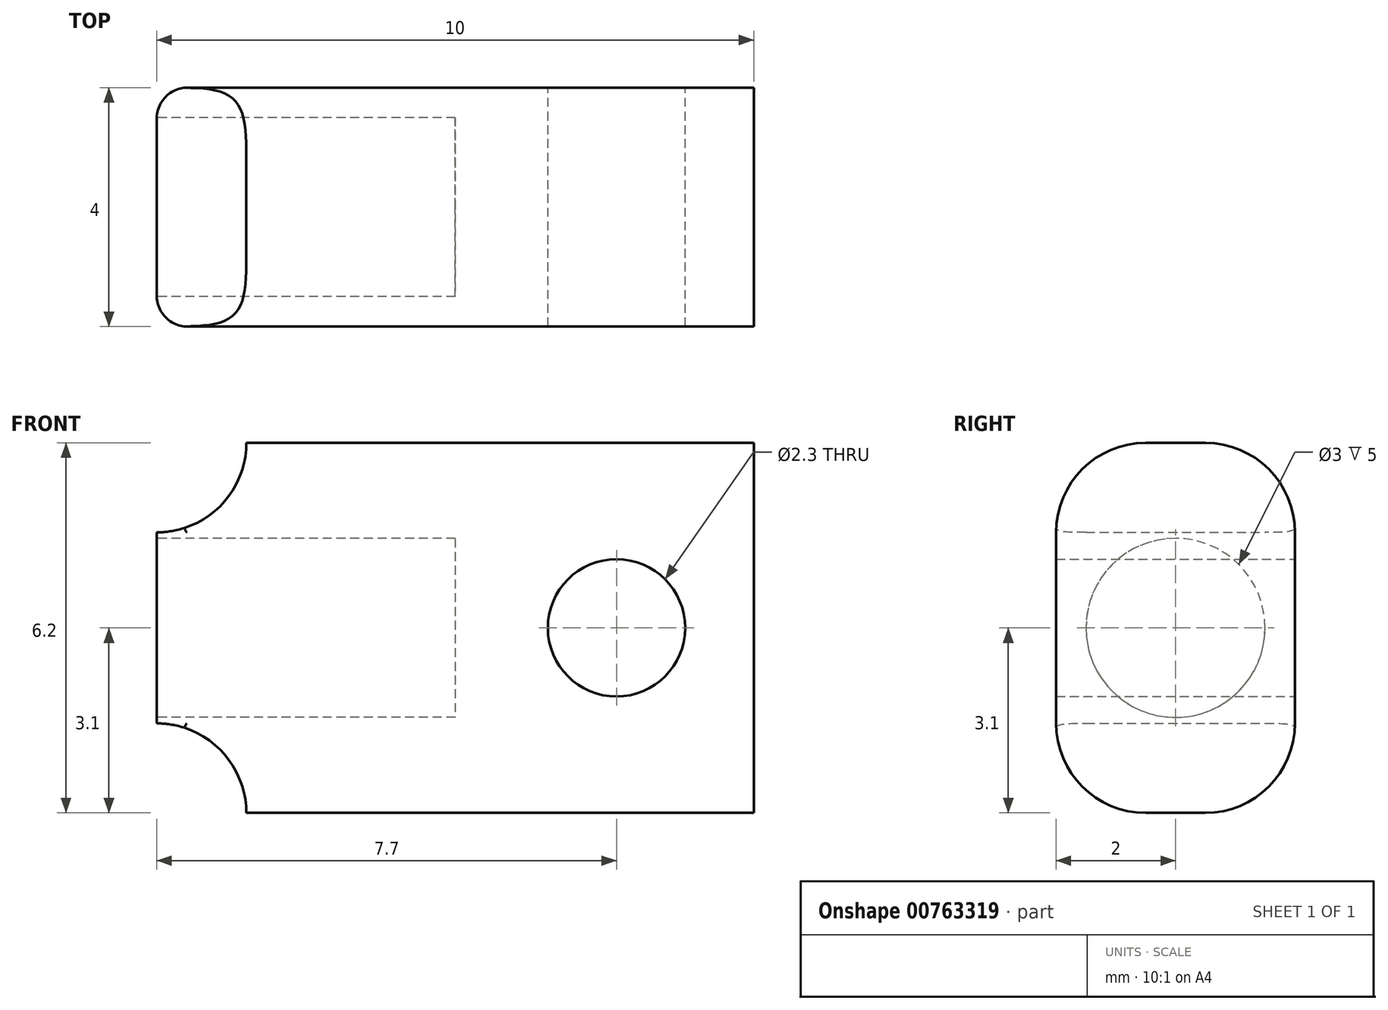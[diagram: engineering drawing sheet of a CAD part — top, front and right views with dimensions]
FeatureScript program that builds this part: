
annotation { "Feature Type Name" : "Feature", "Feature Type Description" : "" }
export const myFeature = defineFeature(function(context is Context, id is Id, definition is map)
    precondition{}
    {
        {
            var Q0;
            Q0=qCreatedBy(makeId("Front.planeOp"),FACE);
            var sketch = newSketch(context, id + "F0", { "sketchPlane" : qUnion([Q0])});
            skLineSegment(sketch, "E0.bottom", {"start": v(5, -3.1) * mm, "end": v(-3.5, -3.1) * mm});
            skLineSegment(sketch, "E0.top", {"start": v(5, 3.1) * mm, "end": v(-3.5, 3.1) * mm});
            skLineSegment(sketch, "E0.left", {"start": v(5, -3.1) * mm, "end": v(5, 3.1) * mm});
            skLineSegment(sketch, "E0.right", {"start": v(-5, -1.6) * mm, "end": v(-5, 1.6) * mm});
            skPoint(sketch, "E0.middle", {"position": v(0, 0) * mm});
            skArc(sketch, "E1", {"start": v(-5, 1.6) * mm, "mid": v(-3.94, 2.04) * mm, "end": v(-3.5, 3.1) * mm});
            skArc(sketch, "E2.MirrorCS", {"start": v(-5, -1.6) * mm, "mid": v(-3.94, -2.04) * mm, "end": v(-3.5, -3.1) * mm});
            skCircle(sketch, "E3", {"center": v(2.7, 0) * mm, "radius": 1.15 * mm});
            skSolve(sketch);
        }
        {
            var Q0;
            Q0=makeQuery(id+"F0.imprint","IMPRINT",FACE,{"disambiguationData":[TD([[makeQuery(id+"F0.imprint","IMPRINT",EDGE,{"derivedFrom":sQuery(id+"F0.wireOp",EDGE,"E0.bottom")}),-1.0]])]});
            extrude(context, id + "F1", {"entities" : qUnion([Q0]), "depth" : 4 * mm, "offsetDistance" : 25 * mm});
        }
        {
            var Q0;
            Q0=makeQuery(id+"F1.opExtrude","SWEPT_FACE",FACE,{"disambiguationData":[OSD([sQuery(id+"F0.wireOp",EDGE,"E0.right")])]});
            var sketch = newSketch(context, id + "F2", { "sketchPlane" : qUnion([Q0])});
            skCircle(sketch, "E4", {"center": v(2, 0) * mm, "radius": 1.5 * mm});
            skPoint(sketch, "E4.centerSnap0", {"position": v(2, 1.6) * mm});
            skSolve(sketch);
        }
        {
            var Q0;
            Q0=makeQuery(id+"F2.imprint","IMPRINT",FACE,{"disambiguationData":[TD([[makeQuery(id+"F2.imprint","IMPRINT",EDGE,{"derivedFrom":sQuery(id+"F2.wireOp",EDGE,"E4")}),1.0]])]});
            extrude(context, id + "F3", {"entities" : qUnion([Q0]), "operationType" : NewBodyOperationType.REMOVE, "oppositeDirection" : true, "depth" : 5 * mm, "offsetDistance" : 25 * mm});
        }
        {
            var Q0;
            Q0=makeQuery(id+"F1.opExtrude","CAP_EDGE",EDGE,{"disambiguationData":[OSD([sQuery(id+"F0.wireOp",EDGE,"E0.top")])],"isStart":true});
            var Q1;
            Q1=makeQuery(id+"F1.opExtrude","CAP_EDGE",EDGE,{"disambiguationData":[OSD([sQuery(id+"F0.wireOp",EDGE,"E0.top")])],"isStart":false});
            var Q2;
            Q2=makeQuery(id+"F1.opExtrude","CAP_EDGE",EDGE,{"disambiguationData":[OSD([sQuery(id+"F0.wireOp",EDGE,"E0.bottom")])],"isStart":false});
            var Q3;
            Q3=makeQuery(id+"F1.opExtrude","CAP_EDGE",EDGE,{"disambiguationData":[OSD([sQuery(id+"F0.wireOp",EDGE,"E0.bottom")])],"isStart":true});
            fillet(context, id + "F4", {"entities" : qUnion([Q0, Q1, Q2, Q3]), "radius" : 1.5 * mm, "tangentPropagation" : true, "allowEdgeOverflow" : false});
        }
        {
            var Q0;
            Q0=makeQuery(id+"F1.opExtrude","CAP_EDGE",EDGE,{"disambiguationData":[OSD([sQuery(id+"F0.wireOp",EDGE,"E0.right")])],"isStart":true});
            var Q1;
            Q1=makeQuery(id+"F1.opExtrude","CAP_EDGE",EDGE,{"disambiguationData":[OSD([sQuery(id+"F0.wireOp",EDGE,"E0.right")])],"isStart":false});
            fillet(context, id + "F5", {"entities" : qUnion([Q0, Q1]), "radius" : 0.5 * mm, "tangentPropagation" : true, "allowEdgeOverflow" : false});
        }
    });
